# Revit family: Zumtobel ARCOS ZF
name_source: partatom
category: Lighting Fixtures
revit_build: Autodesk Revit 2018 (Build: 20190510_1515(x64)
units: mm (PartAtom-declared; Revit-internal decimal feet)

## family parameters
Cut with Voids When Loaded = No
Host = Face
Light Source = No
OmniClass Number = 23.80.70.11
OmniClass Title = Luminaries for Internal Lighting
Part Type = Normal
Room Calculation Point = No
Round Connector Dimension = Use Diameter
Shared = No

## types (3) — shared parameters
Assembly Code = D5020200
Description = Spotlight
Emit Shape Visible in Rendering = No
Lamp = LED
Manufacturer = Zumtobel Lighting
URL = http://www.zumtobel.com
zero-valued in all types: Default Elevation

## per-type parameters (varying)
| type | Apparent Load | Base Height | Body Type | Model |
| ARC ZF L 1800-930 BC 3CU MSP-WFL WH | 45 VA | 135 mm  [stored 0.442913 ft] | Zumtobel ARCOS ZF Body : ARC ZF L 1800-930 BC 3CU MSP-WFL WH | 60715410 |
| ARC ZF M 1040-930 LDO 3CD MSP-WFL WH | 23 VA | 115 mm  [stored 0.377297 ft] | Zumtobel ARCOS ZF Body : ARC ZF M 1040-930 LDO 3CD MSP-WFL WH | 60715325 |
| ARC ZF M 1300-930 BC 3CU SP-WFL WH | 27 VA | 115 mm  [stored 0.377297 ft] | Zumtobel ARCOS ZF Body : ARC ZF M 1300-930 BC 3CU SP-WFL WH | 60715317 |

note: [stored X ft] marks values corroborated as IEEE doubles in the binary element streams (Revit-internal decimal feet)

## geometry (parser evidence)
native form markers: Sweep x6
no freeform markers — native parametric forms only
